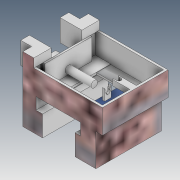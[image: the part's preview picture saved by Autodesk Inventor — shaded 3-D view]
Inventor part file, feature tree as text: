
AUTODESK INVENTOR PART (.ipt)
format: ipt  version: 2021 (Build 250183000, 183)  size: 607,232 bytes
history: native  units: in
note: dims shown in document units (in); Inventor stores cm internally (conversion verified against a paired STEP export)
features: extrude x33, sketch x33, fillet x2, other x1
ambient origin geometry x8: Origin, YZ Plane, XZ Plane, XY Plane, X Axis, Y Axis, Z Axis, Center Point
bodies: Body1 (feature_tree)
feature tree (69):
  other  "Sólido1"
  extrude  "Extrusão1"  Depth=0.1969in
  extrude  "Extrusão2"  Depth=0.3937in
  extrude  "Extrusão3"  Depth=0.0984in
  extrude  "Extrusão4"  Depth=0.1969in
  extrude  "Extrusão5"  Depth=0.3937in
  extrude  "Extrusão6"  Depth=0.0079in
  extrude  "Extrusão7"  Depth=0.0079in
  extrude  "Extrusão8"  Depth=0.0079in
  extrude  "Extrusão10"  Depth=0.0079in
  extrude  "Extrusão11"  Depth=0.0079in
  extrude  "Extrusão12"  Depth=0.0079in
  extrude  "Extrusão13"  Depth=0.0079in
  extrude  "Extrusão16"  Depth=0.0079in
  extrude  "Extrusão17"  Depth=0.1575in
  extrude  "Extrusão18"  Depth=0.0079in
  extrude  "Extrusão19"  Depth=0.0394in
  extrude  "Extrusão20"  Depth=0.0787in
  extrude  "Extrusão21"  Depth=1.1811in TaperAngle=0.0deg
  extrude  "Extrusão22"  Depth=0.3543in
  fillet  "Arredondamento1"  Radius=0.1969in
  extrude  "Extrusão23"  Depth=0.5394in TaperAngle=0.0deg
  extrude  "Extrusão24"  Depth=0.1969in TaperAngle=0.0deg
  fillet  "Arredondamento2"  Radius=0.0591in
  extrude  "Extrusão25"  Depth=0.2559in
  extrude  "Extrusão26"  Depth=0.0315in TaperAngle=0.0deg
  extrude  "Extrusão27"  Depth=0.1575in TaperAngle=0.0deg
  extrude  "Extrusão28"  Depth=0.0394in
  extrude  "Extrusão29"  Depth=0.0394in
  extrude  "Extrusão30"  Depth=0.0394in
  extrude  "Extrusão31"  Depth=0.0394in
  extrude  "Extrusão32"  Depth=0.0394in TaperAngle=0.0deg
  extrude  "Extrusão33"  Depth=0.0197in TaperAngle=0.0deg
  extrude  "Extrusão34"  Depth=0.0787in
  extrude  "Extrusão35"  Depth=0.0787in TaperAngle=0.0deg
  extrude  "Extrusão36"  Depth=0.1181in
  sketch  "Esboço2"  dims[d0=0.1969in d1=0.1969in]
  sketch  "Esboço4"  dims[d2=0.1181in d3=0.3937in]
  sketch  "Esboço5"  dims[d4=0.1969in d5=0.0984in]
  sketch  "Esboço6"  dims[d6=0.3937in d7=0.1969in]
  sketch  "Esboço7"  dims[d8=0.1969in d9=0.3937in]
  sketch  "Esboço8"  dims[d11=0.1969in d12=0.0079in]
  sketch  "Esboço10"  dims[d13=0.0079in d14=0.0079in]
  sketch  "Esboço12"  dims[d15=0.0079in d16=0.0079in]
  sketch  "Esboço15"  dims[d17=0.0079in d19=0.0079in]
  sketch  "Esboço16"  dims[d20=0.0079in d21=0.0079in]
  sketch  "Esboço18"  dims[d22=0.0079in d23=0.0079in]
  sketch  "Esboço20"  dims[d24=0.0079in d25=0.0079in]
  sketch  "Esboço23"  dims[d26=0.0079in d27=0.0079in]
  sketch  "Esboço25"  dims[d28=0.2756in d29=0.1575in]
  sketch  "Esboço26"  dims[d30=0.2756in d31=0.0079in]
  sketch  "Esboço28"  dims[d32=0.0787in d33=0.0394in]
  sketch  "Esboço29"  dims[d34=0.0079in d35=0.0787in]
  sketch  "Esboço30"  dims[d36=0.0394in d37=1.1811in d38=0.0in]
  sketch  "Esboço32"  dims[d39=0.4724in d40=0.3543in d46=0.1969in d47=0.0in]
  sketch  "Esboço33"  dims[d48=0.1181in d49=0.5394in d50=0.0in]
  sketch  "Esboço34"  dims[d51=0.1969in d52=0.0in d53=0.1969in d54=0.0in d55=0.0591in]
  sketch  "Esboço38"  dims[d56=0.1969in d57=0.0in d58=0.2559in]
  sketch  "Esboço39"  dims[d59=0.2559in d60=0.0315in d61=0.0in]
  sketch  "Esboço40"  dims[d62=0.1575in d63=0.0197in d64=0.0in]
  sketch  "Esboço41"  dims[d68=0.1181in d69=0.0in d70=0.0394in]
  sketch  "Esboço42"  dims[d71=0.0394in d73=0.0394in]
  sketch  "Esboço43"  dims[d74=0.3937in d75=0.0in d76=0.0394in]
  sketch  "Esboço44"  dims[d77=0.0in d78=0.0in d79=0.0394in]
  sketch  "Esboço45"  dims[d80=0.0394in d81=0.0394in d82=0.0in]
  sketch  "Esboço46"  dims[d91=0.4134in d92=0.0197in d93=0.0in]
  sketch  "Esboço47"  dims[d94=0.0157in d95=0.0in d96=0.0787in]
  sketch  "Esboço48"  dims[d97=0.0787in d98=0.0626in d99=0.0in]
  sketch  "Esboço50"  dims[d100=0.0197in d101=0.0in d102=0.1181in d103=0.0197in d104=0.0in d105=0.0591in d106=0.0591in d107=0.0591in d108=0.1969in d109=0.0in d110=0.0787in d111=0.0394in d112=0.0787in d114=0.0394in d115=0.0in d116=0.0394in d117=0.0591in d118=0.0591in d119=0.0984in d120=0.3543in d121=0.0in d123=0.0803in d124=0.0984in d125=0.0in d126=0.0079in d128=0.7874in d129=0.1969in d130=0.1969in d131=0.1181in d132=0.3937in d133=0.1969in d134=0.1181in d135=0.1181in d136=0.1969in d137=0.0in d138=0.0039in d139=0.0433in d140=0.0039in d141=0.3858in d142=0.0in d143=0.3937in d144=0.0in d147=0.3858in d148=0.0in d149=0.2283in d150=0.2283in d151=0.0591in d152=0.0in d153=0.0591in d154=0.0in d155=0.1969in d156=0.0in d157=0.3937in d158=0.1969in d159=0.0in d160=0.1969in d161=0.0in d163=0.1575in d164=0.1969in d165=0.0in d166=0.1969in d167=0.0in d170=0.374in d171=0.0in d168=0.0197in d169=0.0344in]
